# Revit family: Casement_41_H_Top_Hung_SD_Standard
name_source: partatom
category: Windows
revit_build: Autodesk Revit 2014 (Build: 20130308_1515(x64)
units: mm (PartAtom-declared; Revit-internal decimal feet)

## types (12) — shared parameters
Corrected Mullion Configuration = 2 mm  [stored 0.00656168 ft]
Custom Sash Height = 502 mm
Description = Window 41mm, Type H, Top hung, Standard sash
Frame Profile Thickness = 41 mm  [stored 0.134514 ft]
Heavy Duty Sash = No
Limit Fixed Pane Height Max = 3000 mm  [stored 9.84252 ft]
Limit Fixed Pane Height Min = 200 mm  [stored 0.656168 ft]
Limit Fixed Pane Width Max = 3000 mm  [stored 9.84252 ft]
Limit Fixed Pane Width Min = 200 mm  [stored 0.656168 ft]
Limit Sash Height Max = 1200 mm  [stored 3.93701 ft]
Limit Sash Height Min = 300 mm  [stored 0.984252 ft]
Limit Sash Width Max = 1500 mm  [stored 4.92126 ft]
Limit Sash Width Min = 300 mm  [stored 0.984252 ft]
Limit Window Width Min = 388 mm
Manufacturer = Crealco
Max System DG Unit Thickness = 25 mm  [stored 0.082021 ft]
Model = Casement 41
Rough Width = 3 mm  [stored 0.00984252 ft]
Sash Side Gap = 44 mm
Standard Mullion Different = No
Standard Sash = Yes
URL = http://www.crealco.co.za
Wall Closure = By host
zero-valued in all types: Custom Frame Offset From Exterior

## per-type parameters (varying)
| type | Clearvue Insulated LowE SHGC Value | Clearvue Insulated LowE U Value | Clearvue Insulated SHGC Value | Clearvue Insulated U Value | Clearvue SHGC Value | Clearvue U Value | Custom Windload | Custom Window Height | Custom Window Width | Energy Advantage SHGC Value | Energy Advantage U Value | Intruderprufe Insulated LowE SHGC Value | Intruderprufe Insulated LowE U Value | Intruderprufe Insulated SHGC Value | Intruderprufe Insulated U Value | Intruderprufe LowE SHGC Value | Intruderprufe LowE U Value | Intruderprufe SHGC Value | Intruderprufe U Value | Toughened Safety SHGC Value | Toughened Safety U Value |
| 41-0615DT-SD-1000Pa | 0.706 | 3.79 | 0.706 | 3.86 | 0.441 | 6.2 | 1000 mm  [stored 3.28084 ft] | 1490 mm  [stored 4.88845 ft] | 590 mm  [stored 1.9357 ft] | 0.397 | 5.1 | 0.587 | 2.78 | 0.588 | 3.1 | 0.37 | 4.96 | 0.415 | 5.88 | 0.441 | 6.2 |
| 41-0615DT-SD-1500Pa | 0.706 | 3.79 | 0.706 | 3.86 | 0.441 | 6.2 | 1500 mm  [stored 4.92126 ft] | 1490 mm  [stored 4.88845 ft] | 590 mm  [stored 1.9357 ft] | 0.397 | 5.1 | 0.587 | 2.78 | 0.588 | 3.1 | 0.37 | 4.96 | 0.415 | 5.88 | 0.441 | 6.2 |
| 41-0615DT-SD-2000Pa | 0.706 | 3.79 | 0.706 | 3.86 | 0.441 | 6.2 | 2000 mm  [stored 6.56168 ft] | 1490 mm  [stored 4.88845 ft] | 590 mm  [stored 1.9357 ft] | 0.397 | 5.1 | 0.587 | 2.78 | 0.588 | 3.1 | 0.37 | 4.96 | 0.415 | 5.88 | 0.441 | 6.2 |
| 41-0915DT-SD-1000Pa | 0.707 | 4.08 | 0.707 | 4.16 | 0.502 | 6.15 | 1000 mm  [stored 3.28084 ft] | 1490 mm  [stored 4.88845 ft] | 890 mm  [stored 2.91995 ft] | 0.451 | 4.83 | 0.587 | 2.98 | 0.589 | 3.31 | 0.42 | 4.7 | 0.473 | 5.8 | 0.502 | 6.15 |
| 41-0915DT-SD-1500Pa | 0.707 | 4.08 | 0.707 | 4.16 | 0.502 | 6.15 | 1500 mm  [stored 4.92126 ft] | 1490 mm  [stored 4.88845 ft] | 890 mm  [stored 2.91995 ft] | 0.451 | 4.83 | 0.587 | 2.98 | 0.589 | 3.31 | 0.42 | 4.7 | 0.473 | 5.8 | 0.502 | 6.15 |
| 41-0915DT-SD-2000Pa | 0.707 | 4.08 | 0.707 | 4.16 | 0.502 | 6.15 | 2000 mm  [stored 6.56168 ft] | 1490 mm  [stored 4.88845 ft] | 890 mm  [stored 2.91995 ft] | 0.451 | 4.83 | 0.587 | 2.98 | 0.589 | 3.31 | 0.42 | 4.7 | 0.473 | 5.8 | 0.502 | 6.15 |
| 41-0618DT-SD-1000Pa | 0.73 | 3.93 | 0.73 | 3.99 | 0.483 | 6.16 | 1000 mm  [stored 3.28084 ft] | 1790 mm  [stored 5.8727 ft] | 590 mm  [stored 1.9357 ft] | 0.434 | 4.98 | 0.607 | 2.79 | 0.608 | 3.06 | 0.404 | 4.83 | 0.455 | 5.85 | 0.483 | 6.16 |
| 41-0618DT-SD-1500Pa | 0.73 | 3.93 | 0.73 | 3.99 | 0.483 | 6.16 | 1500 mm  [stored 4.92126 ft] | 1790 mm  [stored 5.8727 ft] | 590 mm  [stored 1.9357 ft] | 0.434 | 4.98 | 0.607 | 2.79 | 0.608 | 3.06 | 0.404 | 4.83 | 0.455 | 5.85 | 0.483 | 6.16 |
| 41-0618DT-SD-2000Pa | 0.73 | 3.93 | 0.73 | 3.99 | 0.483 | 6.16 | 2000 mm  [stored 6.56168 ft] | 1790 mm  [stored 5.8727 ft] | 590 mm  [stored 1.9357 ft] | 0.434 | 4.98 | 0.607 | 2.79 | 0.608 | 3.06 | 0.404 | 4.83 | 0.455 | 5.85 | 0.483 | 6.16 |
| 41-0918DT-SD-1000Pa | 0.731 | 4.24 | 0.731 | 4.31 | 0.543 | 6.12 | 1000 mm  [stored 3.28084 ft] | 1790 mm  [stored 5.8727 ft] | 890 mm  [stored 2.91995 ft] | 0.487 | 4.72 | 0.607 | 3 | 0.608 | 3.28 | 0.453 | 4.58 | 0.511 | 5.79 | 0.543 | 6.12 |
| 41-0918DT-SD-1500Pa | 0.731 | 4.24 | 0.731 | 4.31 | 0.543 | 6.12 | 1500 mm  [stored 4.92126 ft] | 1790 mm  [stored 5.8727 ft] | 890 mm  [stored 2.91995 ft] | 0.487 | 4.72 | 0.607 | 3 | 0.608 | 3.28 | 0.453 | 4.58 | 0.511 | 5.79 | 0.543 | 6.12 |
| 41-0918DT-SD-2000Pa | 0.731 | 4.24 | 0.731 | 4.31 | 0.543 | 6.12 | 2000 mm  [stored 6.56168 ft] | 1790 mm  [stored 5.8727 ft] | 890 mm  [stored 2.91995 ft] | 0.487 | 4.72 | 0.607 | 3 | 0.608 | 3.28 | 0.453 | 4.58 | 0.511 | 5.79 | 0.543 | 6.12 |

note: [stored X ft] marks values corroborated as IEEE doubles in the binary element streams (Revit-internal decimal feet)

## geometry (parser evidence)
native form markers: Sweep x18
no freeform markers — native parametric forms only
